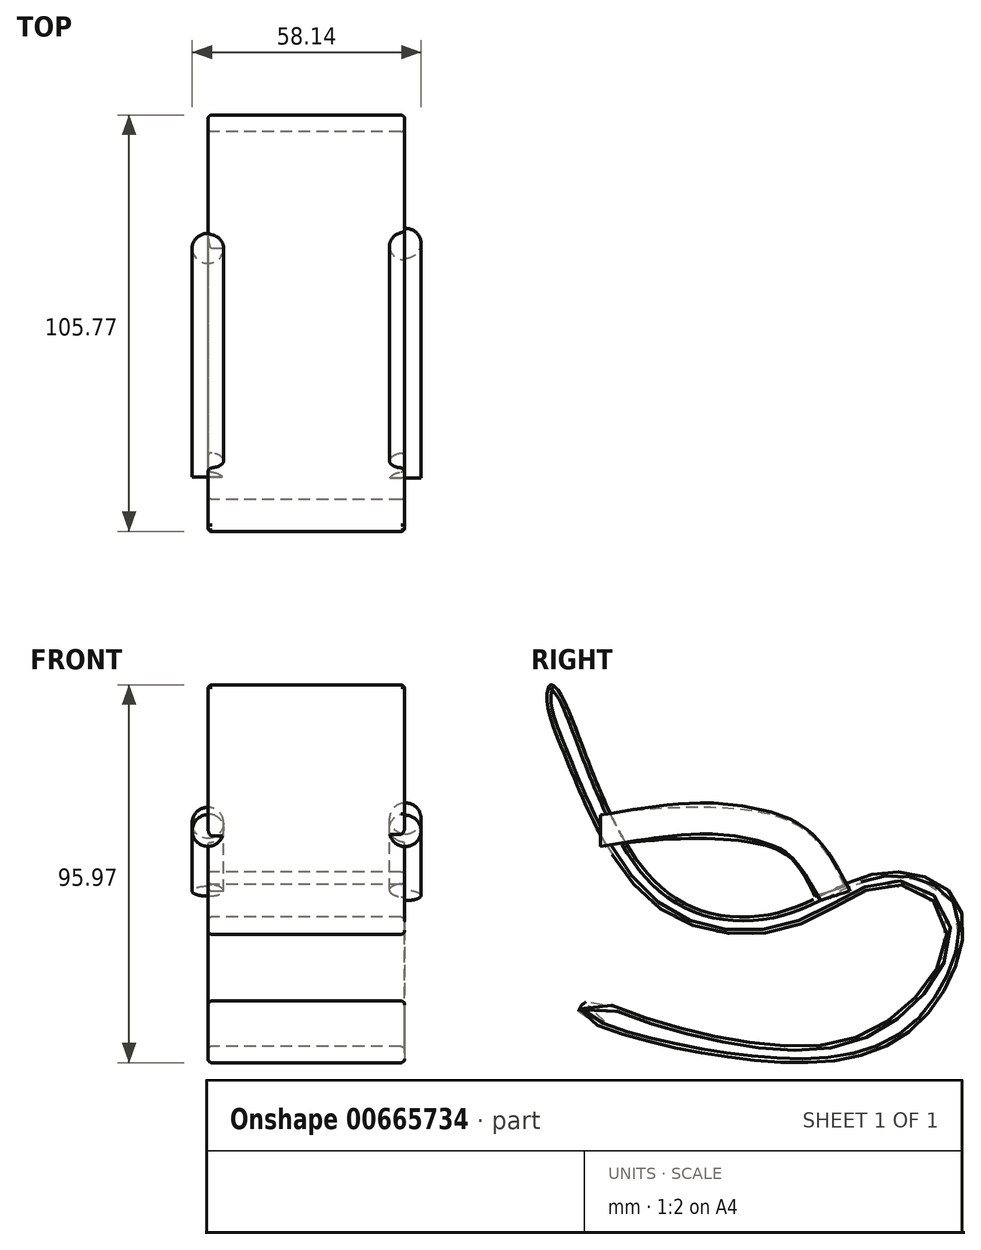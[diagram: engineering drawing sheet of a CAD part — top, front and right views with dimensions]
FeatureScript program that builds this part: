
annotation { "Feature Type Name" : "Feature", "Feature Type Description" : "" }
export const myFeature = defineFeature(function(context is Context, id is Id, definition is map)
    precondition{}
    {
        {
            var Q0;
            Q0=qCreatedBy(makeId("Right.planeOp"),FACE);
            var sketch = newSketch(context, id + "F0", { "sketchPlane" : qUnion([Q0])});
            skFitSpline(sketch, "E0", {"points": [v(-55.25, 59) * mm, v(-32.14, 12.2) * mm, v(1.32, 3.92) * mm, v(26.13, 13.7) * mm, v(45.48, 6.37) * mm, v(40.6, -18.63) * mm, v(10.71, -34.42) * mm, v(-47.36, -24.46) * mm, v(-50.56, -21.07) * mm, v(-48.3, -19) * mm, v(-45.3, -19.38) * mm, v(-42.47, -19.95) * mm, v(-34.4, -22.95) * mm, v(-3.95, -29.9) * mm, v(25, -25.77) * mm, v(42.29, -5.66) * mm, v(39.47, 6.56) * mm, v(26.5, 10.5) * mm, v(3.76, 0) * mm, v(-31.39, 5.62) * mm, v(-54.13, 43.2) * mm, v(-58.64, 56.36) * mm, v(-58.07, 61.25) * mm, v(-55.25, 59) * mm]});
            skSolve(sketch);
        }
        {
            var Q0;
            Q0=makeQuery(id+"F0.imprint","IMPRINT",FACE,{"disambiguationData":[TD([[makeQuery(id+"F0.imprint","IMPRINT",EDGE,{"derivedFrom":sQuery(id+"F0.wireOp",EDGE,"E0")}),-1.0]])]});
            extrude(context, id + "F1", {"entities" : qUnion([Q0]), "depth" : 50 * mm, "offsetDistance" : 25 * mm});
        }
        {
            var Q0;
            Q0=makeQuery(id+"F1.opExtrude","CAP_EDGE",EDGE,{"disambiguationData":[OSD([sQuery(id+"F0.wireOp",EDGE,"E0")])],"isStart":false});
            var Q1;
            Q1=makeQuery(id+"F1.opExtrude","CAP_EDGE",EDGE,{"disambiguationData":[OSD([sQuery(id+"F0.wireOp",EDGE,"E0")])],"isStart":true});
            fillet(context, id + "F2", {"entities" : qUnion([Q0, Q1]), "radius" : 1 * mm, "tangentPropagation" : true, "allowEdgeOverflow" : false});
        }
        {
            var Q0;
            Q0=qCreatedBy(makeId("Right.planeOp"),FACE);
            var sketch = newSketch(context, id + "F3", { "sketchPlane" : qUnion([Q0])});
            skFitSpline(sketch, "E1", {"points": [v(-43.48, 24.99) * mm, v(-31.64, 26.3) * mm, v(-10.97, 26.3) * mm, v(5.39, 21.04) * mm, v(14.22, 7.7) * mm], "startDerivative": vector(50.99, 6.81) * mm, "endDerivative": vector(29.28, -61.35) * mm});
            skSolve(sketch);
        }
        {
            var Q0;
            Q0=qCreatedBy(makeId("Front.planeOp"),FACE);
            cPlane(context, id + "F4", {"entities" : qUnion([Q0]), "cplaneType" : CPlaneType.OFFSET, "offset" : 45 * mm, "width" : 150 * mm, "height" : 150 * mm});
        }
        {
            var Q0;
            Q0=qCreatedBy(id+"F4.planeOp",FACE);
            var sketch = newSketch(context, id + "F5", { "sketchPlane" : qUnion([Q0])});
            skCircle(sketch, "E2", {"center": v(0, 24.38) * mm, "radius": 4 * mm});
            skSolve(sketch);
        }
        {
            var Q0;
            Q0=makeQuery(id+"F5.imprint","IMPRINT",FACE,{"disambiguationData":[TD([[makeQuery(id+"F5.imprint","IMPRINT",EDGE,{"derivedFrom":sQuery(id+"F5.wireOp",EDGE,"E2")}),1.0]])]});
            var Q1;
            Q1=sQuery(id+"F3.wireOp",EDGE,"E1");
            sweep(context, id + "F6", {"operationType" : NewBodyOperationType.ADD, "profiles" : qUnion([Q0]), "path" : qUnion([Q1])});
        }
        {
            var Q0;
            Q0=qCreatedBy(makeId("Right.planeOp"),FACE);
            cPlane(context, id + "F7", {"entities" : qUnion([Q0]), "cplaneType" : CPlaneType.OFFSET, "offset" : 50 * mm, "width" : 150 * mm, "height" : 150 * mm});
        }
        {
            var Q0;
            Q0=qCreatedBy(id+"F4.planeOp",FACE);
            var sketch = newSketch(context, id + "F8", { "sketchPlane" : qUnion([Q0])});
            skCircle(sketch, "E3", {"center": v(50.14, 24.34) * mm, "radius": 4 * mm});
            skSolve(sketch);
        }
        {
            var Q0;
            Q0=qCreatedBy(id+"F7.planeOp",FACE);
            var sketch = newSketch(context, id + "F9", { "sketchPlane" : qUnion([Q0])});
            skFitSpline(sketch, "E4", {"points": [v(-45.2, 24.3) * mm, v(-17.8, 27.45) * mm, v(0, 24.3) * mm, v(7.64, 18.87) * mm, v(14.44, 7.86) * mm], "startDerivative": vector(86.99, 15.05) * mm, "endDerivative": vector(29.3, -54.63) * mm});
            skSolve(sketch);
        }
        {
            var Q0;
            Q0=makeQuery(id+"F8.imprint","IMPRINT",FACE,{"disambiguationData":[TD([[makeQuery(id+"F8.imprint","IMPRINT",EDGE,{"derivedFrom":sQuery(id+"F8.wireOp",EDGE,"E3")}),1.0]])]});
            var Q1;
            Q1=sQuery(id+"F8.wireOp",EDGE,"E3");
            var Q2;
            Q2=sQuery(id+"F9.wireOp",EDGE,"E4");
            sweep(context, id + "F10", {"operationType" : NewBodyOperationType.ADD, "profiles" : qUnion([Q0]), "surfaceProfiles" : qUnion([Q1]), "path" : qUnion([Q2])});
        }
    });
